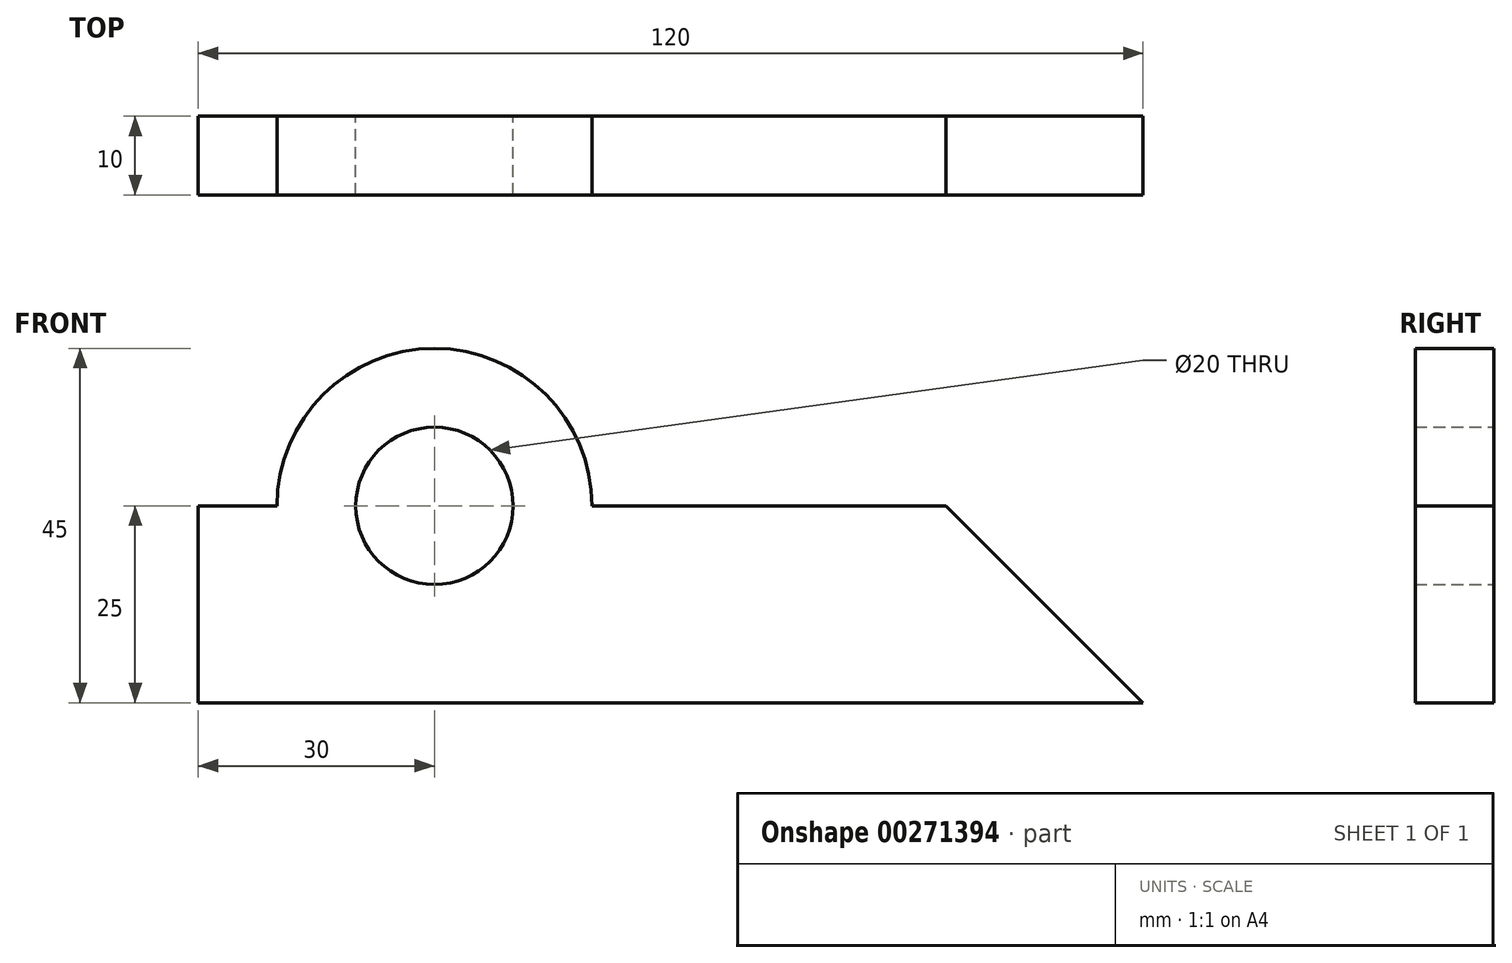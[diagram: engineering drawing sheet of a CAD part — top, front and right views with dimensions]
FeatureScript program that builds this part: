
annotation { "Feature Type Name" : "Feature", "Feature Type Description" : "" }
export const myFeature = defineFeature(function(context is Context, id is Id, definition is map)
    precondition{}
    {
        {
            var Q0;
            Q0=qCreatedBy(makeId("Front.planeOp"),FACE);
            var sketch = newSketch(context, id + "F0", { "sketchPlane" : qUnion([Q0])});
            skLineSegment(sketch, "E0", {"start": v(0, 0) * mm, "end": v(120, 0) * mm});
            skLineSegment(sketch, "E1", {"start": v(0, 0) * mm, "end": v(0, 25) * mm});
            skLineSegment(sketch, "E2", {"start": v(50, 25) * mm, "end": v(95, 25) * mm});
            skLineSegment(sketch, "E3", {"start": v(95, 25) * mm, "end": v(120, 0) * mm});
            skLineSegment(sketch, "E4", {"start": v(0, 25) * mm, "end": v(10, 25) * mm});
            skArc(sketch, "E5", {"start": v(50, 25) * mm, "mid": v(30, 45) * mm, "end": v(10, 25) * mm});
            skCircle(sketch, "E6", {"center": v(30, 25) * mm, "radius": 10 * mm});
            skSolve(sketch);
        }
        {
            var Q0;
            Q0 = qSketchRegion(id + "F0", true);
            extrude(context, id + "F1", {"entities" : qUnion([Q0]), "depth" : 10 * mm});
        }
    });
